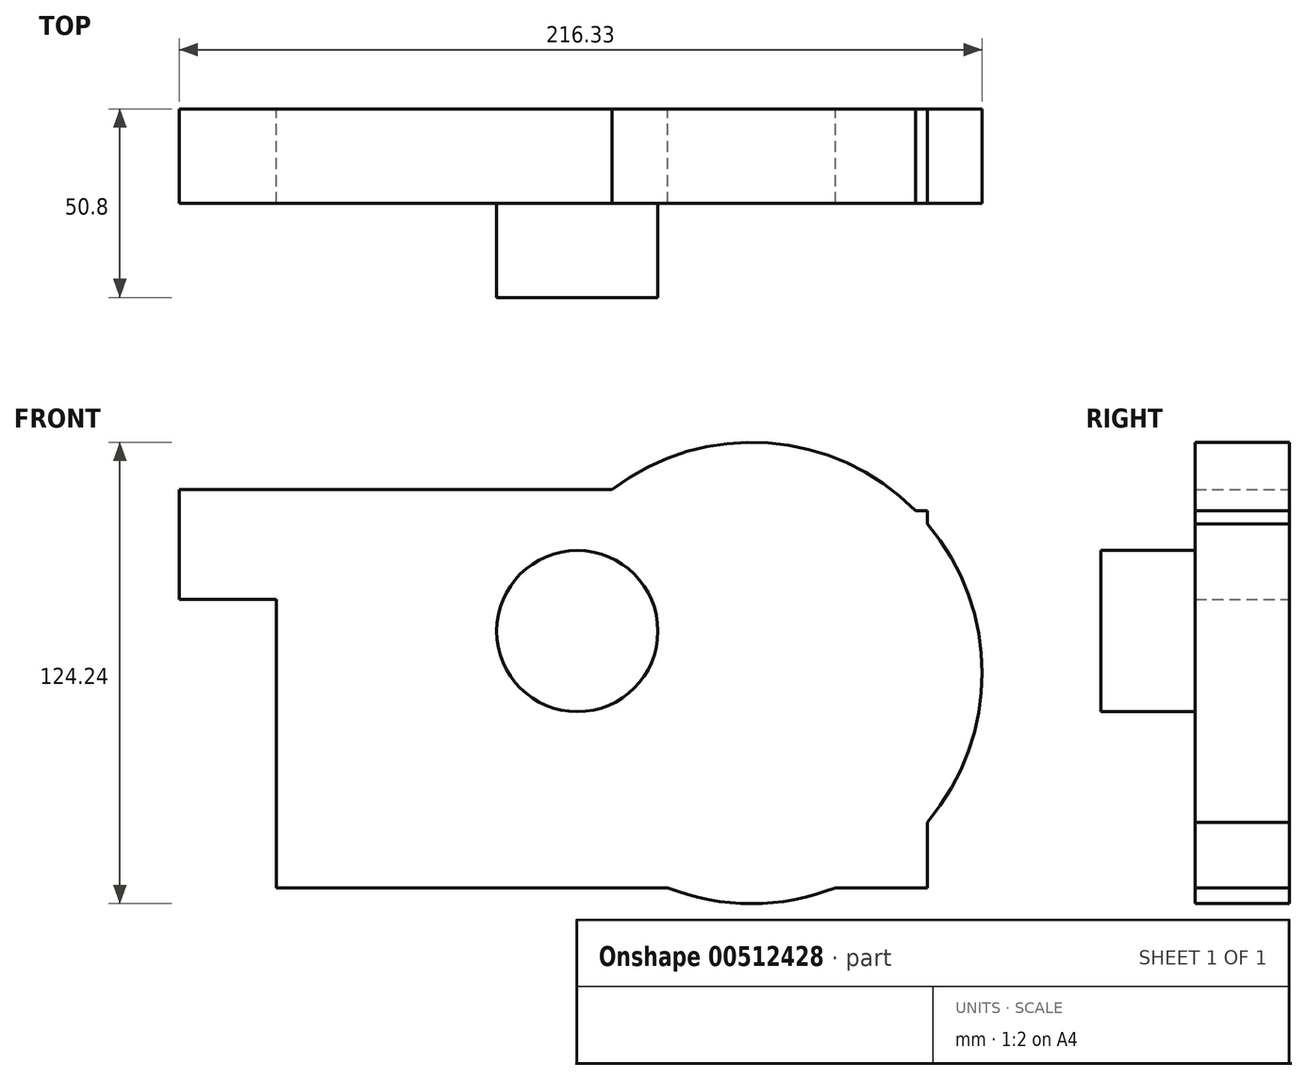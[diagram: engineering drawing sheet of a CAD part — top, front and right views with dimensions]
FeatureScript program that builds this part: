
annotation { "Feature Type Name" : "Feature", "Feature Type Description" : "" }
export const myFeature = defineFeature(function(context is Context, id is Id, definition is map)
    precondition{}
    {
        {
            var Q0;
            Q0=qCreatedBy(makeId("Front.planeOp"),FACE);
            var sketch = newSketch(context, id + "F0", { "sketchPlane" : qUnion([Q0])});
            skLineSegment(sketch, "E0.bottom", {"start": v(-114.9, -57.86) * mm, "end": v(-9.52, -57.86) * mm});
            skLineSegment(sketch, "E0.left", {"start": v(-114.9, -57.86) * mm, "end": v(-114.9, 19.83) * mm});
            skLineSegment(sketch, "E0.right", {"start": v(60.47, -57.86) * mm, "end": v(60.47, -40.2) * mm});
            skLineSegment(sketch, "E1.bottom", {"start": v(-141.1, 49.47) * mm, "end": v(-24.48, 49.47) * mm});
            skLineSegment(sketch, "E1.top", {"start": v(-141.1, 19.83) * mm, "end": v(-114.9, 19.83) * mm});
            skLineSegment(sketch, "E1.left", {"start": v(-141.1, 49.47) * mm, "end": v(-141.1, 19.83) * mm});
            skArc(sketch, "E2", {"start": v(-9.52, -57.86) * mm, "mid": v(13.1, -62.12) * mm, "end": v(35.73, -57.86) * mm});
            skLineSegment(sketch, "E3.trimOffspring", {"start": v(57.3, 43.66) * mm, "end": v(60.47, 43.66) * mm});
            skLineSegment(sketch, "E4.trimOffspring", {"start": v(35.73, -57.86) * mm, "end": v(60.47, -57.86) * mm});
            skArc(sketch, "E5.trimOffspring", {"start": v(60.47, -40.2) * mm, "mid": v(75.23, 0) * mm, "end": v(60.47, 40.2) * mm});
            skLineSegment(sketch, "E6.trimOffspring", {"start": v(60.47, 40.2) * mm, "end": v(60.47, 43.66) * mm});
            skArc(sketch, "E7.trimOffspring", {"start": v(57.3, 43.66) * mm, "mid": v(17.5, 61.97) * mm, "end": v(-24.48, 49.47) * mm});
            skSolve(sketch);
        }
        {
            var Q0;
            Q0 = qSketchRegion(id + "F0", true);
            extrude(context, id + "F1", {"entities" : qUnion([Q0]), "depth" : 50.8 * mm});
        }
        {
            var Q0;
            Q0=makeQuery(id+"F1.opExtrude","CAP_FACE",FACE,{"disambiguationData":[OSD([sQuery(id+"F0.wireOp",EDGE,"E0.bottom"),sQuery(id+"F0.wireOp",EDGE,"E0.left"),sQuery(id+"F0.wireOp",EDGE,"E0.right"),sQuery(id+"F0.wireOp",EDGE,"E1.bottom"),sQuery(id+"F0.wireOp",EDGE,"E1.top"),sQuery(id+"F0.wireOp",EDGE,"E1.left"),sQuery(id+"F0.wireOp",EDGE,"E2"),sQuery(id+"F0.wireOp",EDGE,"E3.trimOffspring"),sQuery(id+"F0.wireOp",EDGE,"E4.trimOffspring"),sQuery(id+"F0.wireOp",EDGE,"E5.trimOffspring"),sQuery(id+"F0.wireOp",EDGE,"E6.trimOffspring"),sQuery(id+"F0.wireOp",EDGE,"E7.trimOffspring")])],"isStart":false});
            var sketch = newSketch(context, id + "F2", { "sketchPlane" : qUnion([Q0])});
            skCircle(sketch, "E8", {"center": v(-33.84, 11.27) * mm, "radius": 21.7 * mm});
            skSolve(sketch);
        }
        {
            var Q0;
            Q0=makeQuery(id+"F2.imprint","IMPRINT",FACE,{"disambiguationData":[TD([[makeQuery(id+"F2.imprint","IMPRINT",EDGE,{"derivedFrom":sQuery(id+"F2.wireOp",EDGE,"E8")}),-1.0]])]});
            extrude(context, id + "F3", {"entities" : qUnion([Q0]), "operationType" : NewBodyOperationType.REMOVE, "oppositeDirection" : true, "depth" : 25.4 * mm});
        }
    });
